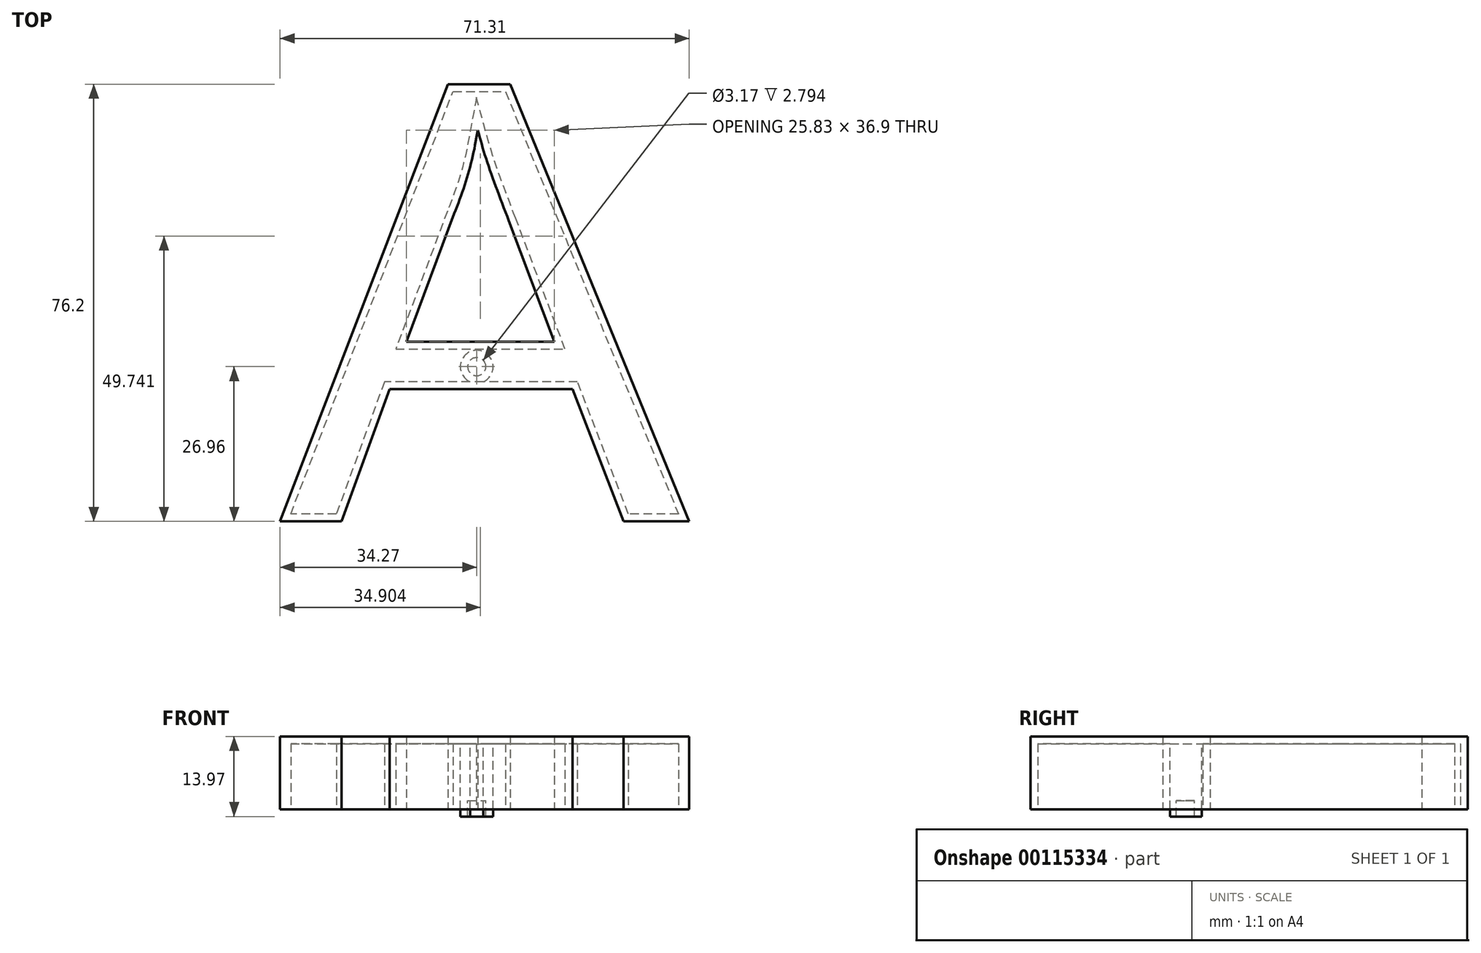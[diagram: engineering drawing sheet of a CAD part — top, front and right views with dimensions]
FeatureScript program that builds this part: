
annotation { "Feature Type Name" : "Feature", "Feature Type Description" : "" }
export const myFeature = defineFeature(function(context is Context, id is Id, definition is map)
    precondition{}
    {
        {
            var Q0;
            Q0=qCreatedBy(makeId("Top.planeOp"),FACE);
            var sketch = newSketch(context, id + "F0", { "sketchPlane" : qUnion([Q0])});
            skLineSegment(sketch, "E0", {"start": v(-34.27, -26.96) * mm, "end": v(-5, 49.24) * mm});
            skLineSegment(sketch, "E1", {"start": v(-5, 49.24) * mm, "end": v(5.86, 49.24) * mm});
            skLineSegment(sketch, "E2", {"start": v(5.86, 49.24) * mm, "end": v(37.04, -26.96) * mm});
            skLineSegment(sketch, "E3", {"start": v(37.04, -26.96) * mm, "end": v(25.56, -26.96) * mm});
            skLineSegment(sketch, "E4", {"start": v(25.56, -26.96) * mm, "end": v(16.67, -3.88) * mm});
            skLineSegment(sketch, "E5", {"start": v(16.67, -3.88) * mm, "end": v(-15.2, -3.88) * mm});
            skLineSegment(sketch, "E6", {"start": v(-15.2, -3.88) * mm, "end": v(-23.56, -26.96) * mm});
            skLineSegment(sketch, "E7", {"start": v(-23.56, -26.96) * mm, "end": v(-34.27, -26.96) * mm});
            skFitSpline(sketch, "E8", {"points": [v(5.6, 25.43) * mm, v(3.17, 31.84) * mm, v(1.37, 37.1) * mm, v(0.2, 41.23) * mm]});
            skFitSpline(sketch, "E9", {"points": [v(0.2, 41.23) * mm, v(-0.78, 36.35) * mm, v(-2.15, 31.5) * mm, v(-3.91, 26.68) * mm]});
            skLineSegment(sketch, "E10", {"start": v(-12.28, 4.33) * mm, "end": v(13.55, 4.33) * mm});
            skLineSegment(sketch, "E11", {"start": v(13.55, 4.33) * mm, "end": v(5.6, 25.43) * mm});
            skLineSegment(sketch, "E12", {"start": v(-3.91, 26.68) * mm, "end": v(-12.28, 4.33) * mm});
            skSolve(sketch);
        }
        {
            var Q0;
            Q0=makeQuery(id+"F0.imprint","IMPRINT",FACE,{"disambiguationData":[TD([[makeQuery(id+"F0.imprint","IMPRINT",EDGE,{"derivedFrom":sQuery(id+"F0.wireOp",EDGE,"E0")}),-1.0]])]});
            extrude(context, id + "F1", {"entities" : qUnion([Q0]), "depth" : 12.7 * mm});
        }
        {
            var Q0;
            Q0=makeQuery(id+"F1.opExtrude","CAP_FACE",FACE,{"disambiguationData":[OSD([sQuery(id+"F0.wireOp",EDGE,"E0"),sQuery(id+"F0.wireOp",EDGE,"E1"),sQuery(id+"F0.wireOp",EDGE,"E2"),sQuery(id+"F0.wireOp",EDGE,"E3"),sQuery(id+"F0.wireOp",EDGE,"E4"),sQuery(id+"F0.wireOp",EDGE,"E5"),sQuery(id+"F0.wireOp",EDGE,"E6"),sQuery(id+"F0.wireOp",EDGE,"E7"),sQuery(id+"F0.wireOp",EDGE,"E8"),sQuery(id+"F0.wireOp",EDGE,"E9"),sQuery(id+"F0.wireOp",EDGE,"E10"),sQuery(id+"F0.wireOp",EDGE,"E11"),sQuery(id+"F0.wireOp",EDGE,"E12")])],"isStart":true});
            shell(context, id + "F2", {"entities" : qUnion([Q0]), "thickness" : 1.27 * mm});
        }
        {
            var Q0;
            {var subQ0=sQuery(id+"F0.wireOp",EDGE,"E12");var subQ1=sQuery(id+"F0.wireOp",EDGE,"E11");var subQ2=sQuery(id+"F0.wireOp",EDGE,"E10");var subQ3=sQuery(id+"F0.wireOp",EDGE,"E9");var subQ4=sQuery(id+"F0.wireOp",EDGE,"E8");var subQ5=sQuery(id+"F0.wireOp",EDGE,"E7");var subQ6=sQuery(id+"F0.wireOp",EDGE,"E6");var subQ7=sQuery(id+"F0.wireOp",EDGE,"E5");var subQ8=sQuery(id+"F0.wireOp",EDGE,"E4");var subQ9=sQuery(id+"F0.wireOp",EDGE,"E3");var subQ10=sQuery(id+"F0.wireOp",EDGE,"E2");var subQ11=sQuery(id+"F0.wireOp",EDGE,"E1");var subQ12=sQuery(id+"F0.wireOp",EDGE,"E0");Q0=makeQuery(id+"F2.opShell","OFFSET_FACE",FACE,{"disambiguationData":[OSD([subQ12,subQ11,subQ10,subQ9,subQ8,subQ7,subQ6,subQ5,subQ4,subQ3,subQ2,subQ1,subQ0]),TDD([makeQuery(id+"F1.opExtrude","CAP_FACE",FACE,{"disambiguationData":[OSD([subQ12,subQ11,subQ10,subQ9,subQ8,subQ7,subQ6,subQ5,subQ4,subQ3,subQ2,subQ1,subQ0])],"isStart":false})])]});}
            var sketch = newSketch(context, id + "F3", { "sketchPlane" : qUnion([Q0])});
            skCircle(sketch, "E13", {"center": v(0, 0) * mm, "radius": 1.59 * mm});
            skCircle(sketch, "E14.0", {"center": v(0, 0) * mm, "radius": 2.86 * mm});
            skSolve(sketch);
        }
        {
            var Q0;
            Q0=makeQuery(id+"F3.imprint","IMPRINT",FACE,{"disambiguationData":[TD([[makeQuery(id+"F3.imprint","IMPRINT",EDGE,{"derivedFrom":sQuery(id+"F3.wireOp",EDGE,"E13")}),-1.0]])]});
            extrude(context, id + "F4", {"entities" : qUnion([Q0]), "operationType" : NewBodyOperationType.ADD, "depth" : 12.7 * mm});
        }
        {
            var Q0;
            {var subQ0=sQuery(id+"F0.wireOp",EDGE,"E12");var subQ1=sQuery(id+"F0.wireOp",EDGE,"E11");var subQ2=sQuery(id+"F0.wireOp",EDGE,"E10");var subQ3=sQuery(id+"F0.wireOp",EDGE,"E9");var subQ4=sQuery(id+"F0.wireOp",EDGE,"E8");var subQ5=sQuery(id+"F0.wireOp",EDGE,"E7");var subQ6=sQuery(id+"F0.wireOp",EDGE,"E6");var subQ7=sQuery(id+"F0.wireOp",EDGE,"E5");var subQ8=sQuery(id+"F0.wireOp",EDGE,"E4");var subQ9=sQuery(id+"F0.wireOp",EDGE,"E3");var subQ10=sQuery(id+"F0.wireOp",EDGE,"E2");var subQ11=sQuery(id+"F0.wireOp",EDGE,"E1");var subQ12=sQuery(id+"F0.wireOp",EDGE,"E0");Q0=makeQuery(id+"F4.boolean.opBoolean","SPLIT",FACE,{"disambiguationData":[TD([makeQuery(id+"F4.opExtrude","SWEPT_FACE",FACE,{"disambiguationData":[OSD([sQuery(id+"F3.wireOp",EDGE,"E13")])]})])],"derivedFrom":makeQuery(id+"F2.opShell","OFFSET_FACE",FACE,{"disambiguationData":[OSD([subQ12,subQ11,subQ10,subQ9,subQ8,subQ7,subQ6,subQ5,subQ4,subQ3,subQ2,subQ1,subQ0]),TDD([makeQuery(id+"F1.opExtrude","CAP_FACE",FACE,{"disambiguationData":[OSD([subQ12,subQ11,subQ10,subQ9,subQ8,subQ7,subQ6,subQ5,subQ4,subQ3,subQ2,subQ1,subQ0])],"isStart":false})])]})});}
            extrude(context, id + "F5", {"entities" : qUnion([Q0]), "operationType" : NewBodyOperationType.ADD, "depth" : 9.9 * mm});
        }
    });
